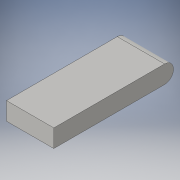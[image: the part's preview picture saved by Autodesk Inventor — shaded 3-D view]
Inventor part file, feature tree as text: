
AUTODESK INVENTOR PART (.ipt)
format: ipt  version: 2016 (Build 200138000, 138)  size: 90,624 bytes
history: native  units: in
note: dims shown in document units (in); Inventor stores cm internally (conversion verified against a paired STEP export)
features: extrude x1, fillet x1, sketch x1
ambient origin geometry x8: Origin, YZ Plane, XZ Plane, XY Plane, X Axis, Y Axis, Z Axis, Center Point
bodies: Solid1 (feature_tree)
feature tree (3):
  extrude  "Extrusion1"  Depth=2.648in
  fillet  "Fillet1"  Radius=1.0in
  sketch  "Sketch1"  dims[d0=6.7in d1=2.648in d2=1.0in d3=0.0in d4=0.5in]
